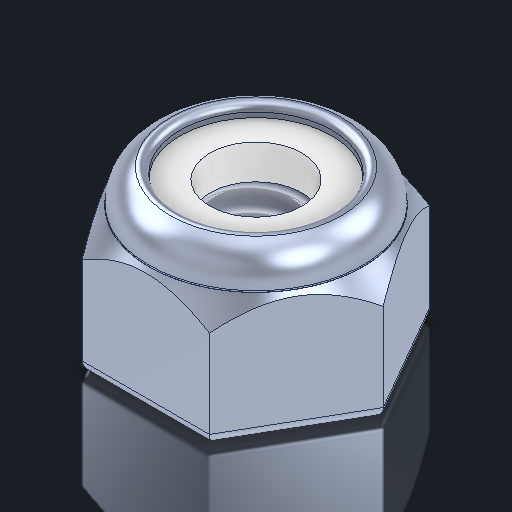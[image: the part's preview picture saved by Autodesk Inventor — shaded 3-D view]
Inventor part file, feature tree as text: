
AUTODESK INVENTOR PART (.ipt)
format: ipt  version: 2023.2 (Build 272271030, 271C)  size: 238,080 bytes
history: native  units: in
note: dims shown in document units (in); Inventor stores cm internally (conversion verified against a paired STEP export)
features: other x4, plane x2, sketch x1
ambient origin geometry x8: Origin, YZ Plane, XZ Plane, XY Plane, X Axis, Y Axis, Z Axis, Center Point
bodies: Body1 (feature_tree)
feature tree (7):
  other  "Nut Nylock_CPY.ipt"
  other  "NONE::Nut Nylock_CPY.ipt"
  other  "TaggingFeature1"
  sketch  "Sketch1"  dims[d0=0.3937in]
  plane  "Work Plane1"
  plane  "Work Plane2"
  parser-record x1  (decoder bookkeeping rows leaked as tree rows — omitted from the tree; the rows remain in map.json)
